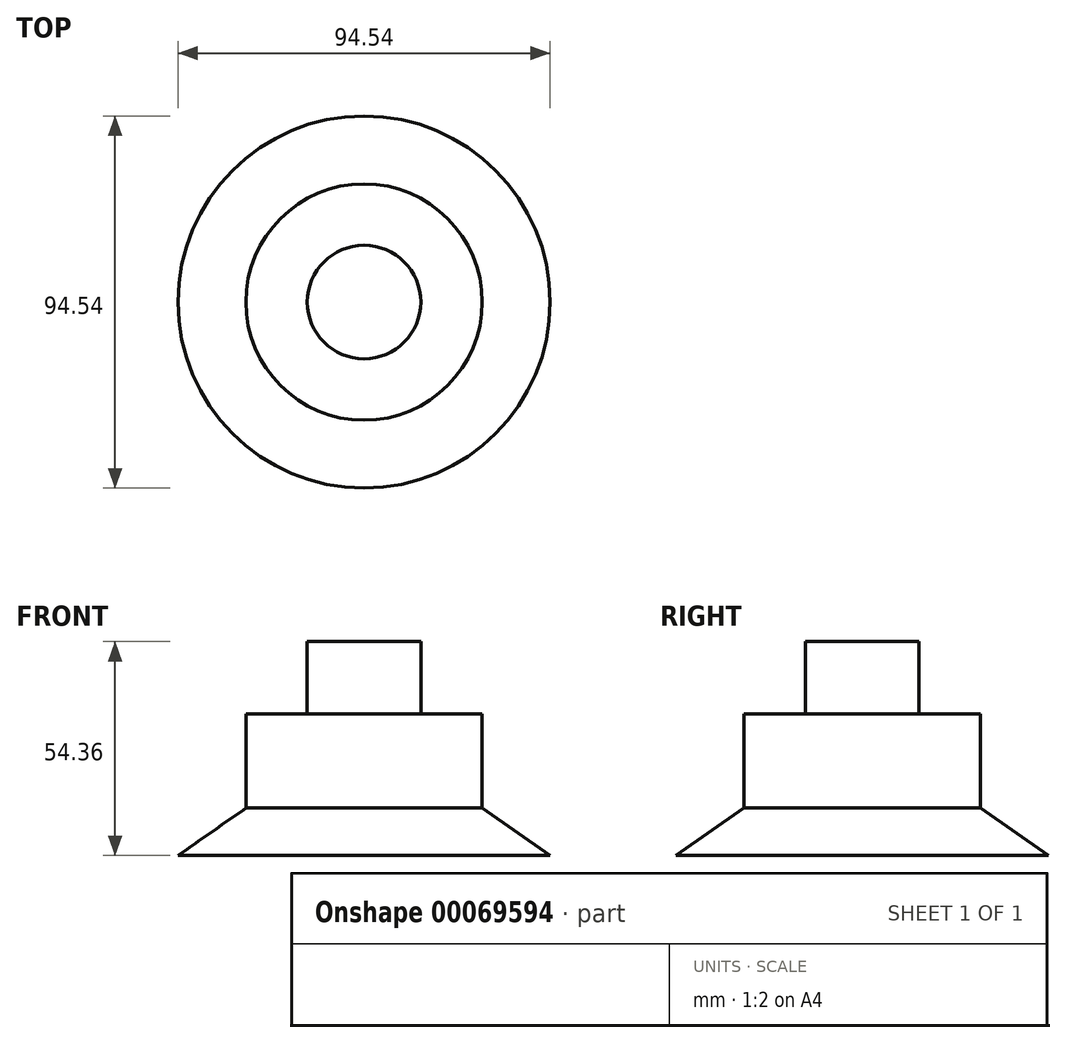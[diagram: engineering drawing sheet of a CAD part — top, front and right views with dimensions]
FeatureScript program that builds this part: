
annotation { "Feature Type Name" : "Feature", "Feature Type Description" : "" }
export const myFeature = defineFeature(function(context is Context, id is Id, definition is map)
    precondition{}
    {
        {
            var Q0;
            Q0=qCreatedBy(makeId("Front.planeOp"),FACE);
            var sketch = newSketch(context, id + "F0", { "sketchPlane" : qUnion([Q0])});
            skLineSegment(sketch, "E0", {"start": v(0, -77.89) * mm, "end": v(0, 80) * mm, "construction": true});
            skLineSegment(sketch, "E1", {"start": v(0, 67.95) * mm, "end": v(14.42, 67.95) * mm});
            skLineSegment(sketch, "E2", {"start": v(14.42, 67.95) * mm, "end": v(14.42, 49.52) * mm});
            skLineSegment(sketch, "E3", {"start": v(14.42, 49.52) * mm, "end": v(30.02, 49.52) * mm});
            skLineSegment(sketch, "E4", {"start": v(30.02, 49.52) * mm, "end": v(30.02, 25.64) * mm});
            skLineSegment(sketch, "E5", {"start": v(30.02, 25.64) * mm, "end": v(47.27, 13.59) * mm});
            skLineSegment(sketch, "E6", {"start": v(47.27, 13.59) * mm, "end": v(0, 13.59) * mm});
            skLineSegment(sketch, "E7", {"start": v(0, 13.59) * mm, "end": v(0, 67.95) * mm});
            skSolve(sketch);
        }
        {
            var Q0;
            Q0=makeQuery(id+"F0.imprint","IMPRINT",FACE,{"disambiguationData":[TD([[makeQuery(id+"F0.imprint","IMPRINT",EDGE,{"derivedFrom":sQuery(id+"F0.wireOp",EDGE,"E1")}),-1.0]])]});
            var Q1;
            Q1=sQuery(id+"F0.wireOp",EDGE,"E0");
            revolve(context, id + "F1", {"entities" : qUnion([Q0]), "axis" : qUnion([Q1]), "revolveType" : RevolveType.FULL});
        }
    });
